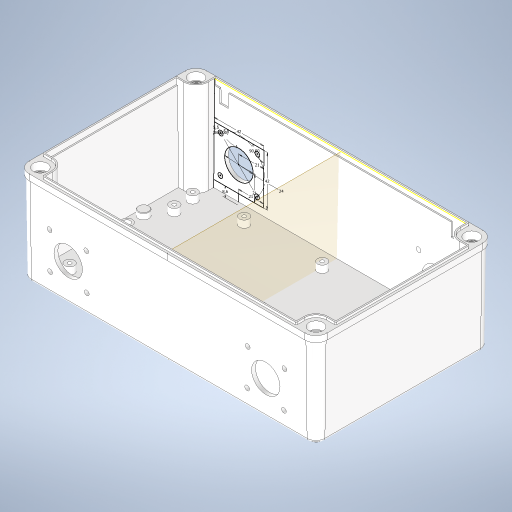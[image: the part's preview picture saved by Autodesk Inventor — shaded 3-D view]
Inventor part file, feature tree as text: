
AUTODESK INVENTOR PART (.ipt)
format: ipt  version: 2024 (Build 280153000, 153)  size: 2,229,760 bytes
history: native  units: in
note: dims shown in document units (in); Inventor stores cm internally (conversion verified against a paired STEP export)
features: other x3, extrude x2, sketch x1, plane x1, mirror x1
ambient origin geometry x8: Origin, YZ Plane, XZ Plane, XY Plane, X Axis, Y Axis, Z Axis, Center Point
bodies: Solid1 (feature_tree)
feature tree (8):
  other  "ORCF FILLETS"
  other  "LOCATING FASTENING BODY CIRCLE PATTERN AXIS"
  other  "Plane1"
  sketch  "Sketch2"  dims[d1=0.3386in d2=0.8268in d3=1.6535in d4=1.6535in d5=90.0deg d6=0.9449in d7=0.8268in d8=0.8268in d9=0.1575in d10=0.2165in d11=0.2165in d12=1.5748in d14=360.0deg d16=0.3937in d17=0.0in d19=-4.9568in d20=0.3937in d21=0.0in]
  extrude  "Extrusion1"  Depth=0.3937in
  plane  "Work Plane3"
  extrude  "Extrusion2"  Depth=0.3937in
  mirror  "Mirror1"
